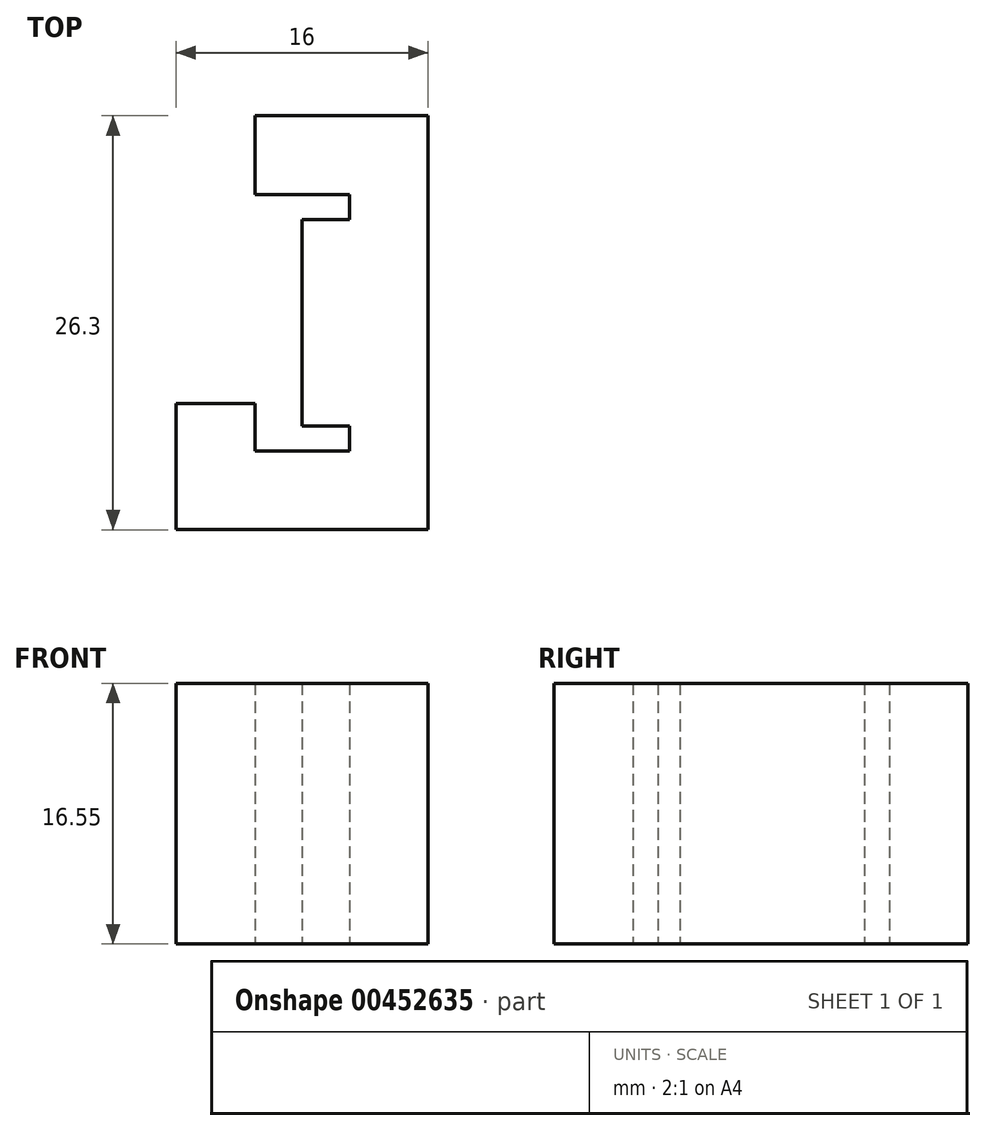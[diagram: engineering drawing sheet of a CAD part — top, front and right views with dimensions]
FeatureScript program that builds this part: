
annotation { "Feature Type Name" : "Feature", "Feature Type Description" : "" }
export const myFeature = defineFeature(function(context is Context, id is Id, definition is map)
    precondition{}
    {
        {
            var Q0;
            Q0=qCreatedBy(makeId("Top.planeOp"),FACE);
            var sketch = newSketch(context, id + "F0", { "sketchPlane" : qUnion([Q0])});
            skLineSegment(sketch, "E0", {"start": v(28.94, -21.96) * mm, "end": v(28.94, -29.96) * mm});
            skLineSegment(sketch, "E1", {"start": v(28.94, -29.96) * mm, "end": v(44.94, -29.96) * mm});
            skLineSegment(sketch, "E2", {"start": v(44.94, -29.96) * mm, "end": v(44.94, -3.66) * mm});
            skLineSegment(sketch, "E3", {"start": v(44.94, -3.66) * mm, "end": v(33.94, -3.66) * mm});
            skLineSegment(sketch, "E4", {"start": v(33.94, -8.66) * mm, "end": v(39.94, -8.66) * mm});
            skLineSegment(sketch, "E5", {"start": v(39.94, -8.66) * mm, "end": v(39.94, -10.26) * mm});
            skLineSegment(sketch, "E6", {"start": v(39.94, -10.26) * mm, "end": v(36.94, -10.26) * mm});
            skLineSegment(sketch, "E7", {"start": v(36.94, -10.26) * mm, "end": v(36.94, -23.36) * mm});
            skLineSegment(sketch, "E8", {"start": v(36.94, -23.36) * mm, "end": v(39.94, -23.36) * mm});
            skLineSegment(sketch, "E9", {"start": v(39.94, -23.36) * mm, "end": v(39.94, -24.96) * mm});
            skLineSegment(sketch, "E10", {"start": v(39.94, -24.96) * mm, "end": v(33.94, -24.96) * mm});
            skLineSegment(sketch, "E11", {"start": v(33.94, -24.96) * mm, "end": v(33.94, -21.96) * mm});
            skLineSegment(sketch, "E12", {"start": v(33.94, -21.96) * mm, "end": v(28.94, -21.96) * mm});
            skLineSegment(sketch, "E13", {"start": v(33.94, -3.66) * mm, "end": v(33.94, -8.66) * mm});
            skPoint(sketch, "E14.end.orphan", {"position": v(28.94, -8.66) * mm});
            skPoint(sketch, "E15.orphan", {"position": v(28.94, -3.66) * mm});
            skSolve(sketch);
        }
        {
            var Q0;
            Q0 = qSketchRegion(id + "F0", true);
            extrude(context, id + "F1", {"entities" : qUnion([Q0]), "depth" : 16.55 * mm});
        }
    });
